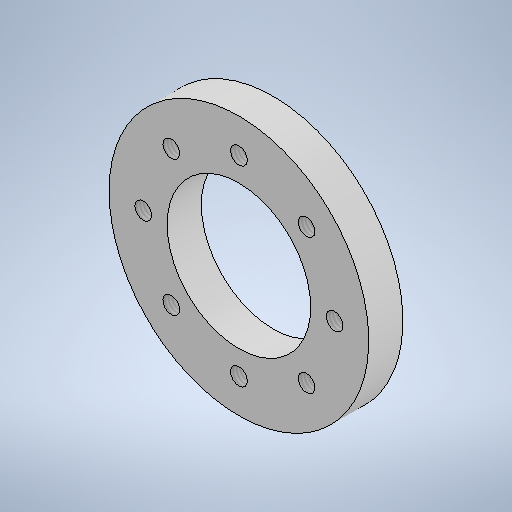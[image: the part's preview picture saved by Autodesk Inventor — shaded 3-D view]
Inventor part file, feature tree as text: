
AUTODESK INVENTOR PART (.ipt)
format: ipt  version: 2025 (Build 290162010, 162A)  size: 261,632 bytes
history: native  units: mm
features: sketch x2, extrude x1, hole x1, pattern_circular x1
ambient origin geometry x8: Origin, YZ Plane, XZ Plane, XY Plane, X Axis, Y Axis, Z Axis, Center Point
bodies: Solid1 (feature_tree)
feature tree (5):
  extrude  "Extrusion1"  Depth=21.0mm
  hole  "Hole1"  [1 undecoded]
  pattern_circular  "Circular Pattern1"  Count=8 Angle=360.0deg
  sketch  "Sketch1"  dims[d0=38.0mm d1=21.0mm]
  sketch  "Sketch2"  dims[d2=5.0mm d3=0.0mm d4=28.0mm d5=2.459mm d6=6.0mm d7=4.0mm d8=2.0mm d9=90.0deg d10=8.8mm d11=0.0mm d12=80.0mm d13=360.0deg]
note: 1 required parameter value undecoded (feature->parameter linkage not recoverable at this tier; creation-order binding heuristic only, values carry confidence <= 0.55)
